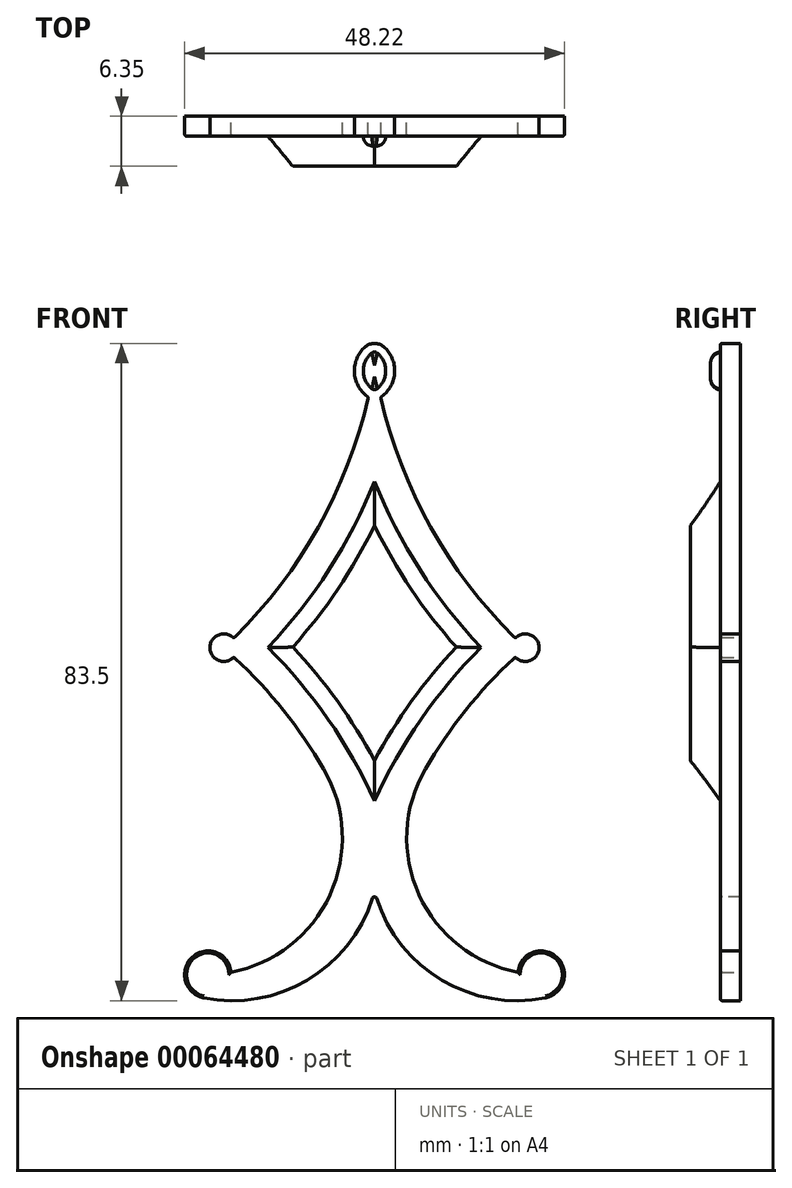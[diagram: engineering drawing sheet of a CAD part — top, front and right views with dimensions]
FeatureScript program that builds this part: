
annotation { "Feature Type Name" : "Feature", "Feature Type Description" : "" }
export const myFeature = defineFeature(function(context is Context, id is Id, definition is map)
    precondition{}
    {
        {
            var Q0;
            Q0=qCreatedBy(makeId("Front.planeOp"),FACE);
            var sketch = newSketch(context, id + "F0", { "sketchPlane" : qUnion([Q0])});
            skArc(sketch, "E0", {"start": v(-17.9, 1.2) * mm, "mid": v(-7.14, 15.28) * mm, "end": v(-0.78, 31.81) * mm});
            skArc(sketch, "E1", {"start": v(-6.45, -15.43) * mm, "mid": v(-11.63, -7.88) * mm, "end": v(-17.87, -1.17) * mm});
            skArc(sketch, "E2", {"start": v(-18.24, -41.23) * mm, "mid": v(-5.65, -31.39) * mm, "end": v(-6.45, -15.43) * mm});
            skArc(sketch, "E3", {"start": v(-17.9, 1.2) * mm, "mid": v(-20.9, -0.02) * mm, "end": v(-17.87, -1.17) * mm});
            skArc(sketch, "E4", {"start": v(-21.74, -44.48) * mm, "mid": v(-8.2, -42.03) * mm, "end": v(0, -30.98) * mm});
            skEllipticalArc(sketch, "E5", {});
            skLineSegment(sketch, "E6", {"start": v(0, 77.82) * mm, "end": v(0, -71.34) * mm, "construction": true});
            skArc(sketch, "E7.MirrorCS", {"start": v(17.9, 1.2) * mm, "mid": v(7.14, 15.28) * mm, "end": v(0.78, 31.81) * mm});
            skArc(sketch, "E8.MirrorCS", {"start": v(6.45, -15.43) * mm, "mid": v(11.63, -7.88) * mm, "end": v(17.87, -1.17) * mm});
            skArc(sketch, "E9.MirrorCS", {"start": v(18.24, -41.23) * mm, "mid": v(5.65, -31.39) * mm, "end": v(6.45, -15.43) * mm});
            skArc(sketch, "E10.MirrorCS", {"start": v(21.74, -44.48) * mm, "mid": v(8.2, -42.03) * mm, "end": v(0, -30.98) * mm});
            skEllipticalArc(sketch, "E11.MirrorC", {});
            skArc(sketch, "E12", {"start": v(0, 38.93) * mm, "mid": v(-2.54, 35.6) * mm, "end": v(-0.78, 31.81) * mm});
            skArc(sketch, "E13.MirrorCS", {"start": v(0, 38.93) * mm, "mid": v(2.54, 35.6) * mm, "end": v(0.78, 31.81) * mm});
            skPoint(sketch, "E14.orphan", {"position": v(0, -30.98) * mm});
            skPoint(sketch, "E15.orphan", {"position": v(0, 35.8) * mm});
            skArc(sketch, "E16.MirrorCS", {"start": v(17.9, 1.2) * mm, "mid": v(20.9, -0.02) * mm, "end": v(17.87, -1.17) * mm});
            const initialGuessF0  = {"E5": [-0.02116856537759304, -0.04152892157435417, 1, 0, 0.002945323460980625, 0.0030059937877719195, 0.09832466558772346, 4.51858815046972], "E11.MirrorC": [0.02116856537759304, -0.04152892157435417, -1, 0, 0.002945323460980625, 0.0030059937877719195, 1.764597156709867, 6.184860641591863], "E11.MirrorC": [0.02116856537759304, -0.04152892157435417, -1, 0, 0.002945323460980625, 0.0030059937877719195, 1.764597156709867, 6.1848606415918645]};
            skSetInitialGuess(sketch, initialGuessF0);
            skSolve(sketch);
        }
        {
            var Q0;
            Q0 = qSketchRegion(id + "F0", true);
            extrude(context, id + "F1", {"entities" : qUnion([Q0]), "depth" : 2.54 * mm});
        }
        {
            var Q0;
            Q0=makeQuery(id+"F1.opExtrude","CAP_FACE",FACE,{"disambiguationData":[OSD([sQuery(id+"F0.wireOp",EDGE,"E0"),sQuery(id+"F0.wireOp",EDGE,"E1"),sQuery(id+"F0.wireOp",EDGE,"E2"),sQuery(id+"F0.wireOp",EDGE,"E3"),sQuery(id+"F0.wireOp",EDGE,"E4"),sQuery(id+"F0.wireOp",EDGE,"E5"),sQuery(id+"F0.wireOp",EDGE,"E7.MirrorCS"),sQuery(id+"F0.wireOp",EDGE,"E8.MirrorCS"),sQuery(id+"F0.wireOp",EDGE,"E12"),sQuery(id+"F0.wireOp",EDGE,"E13.MirrorCS"),sQuery(id+"F0.wireOp",EDGE,"E16.MirrorCS"),sQuery(id+"F0.wireOp",EDGE,"E10.MirrorCS"),sQuery(id+"F0.wireOp",EDGE,"E11.MirrorC"),sQuery(id+"F0.wireOp",EDGE,"E9.MirrorCS")])],"isStart":false});
            var sketch = newSketch(context, id + "F2", { "sketchPlane" : qUnion([Q0])});
            skArc(sketch, "E17", {"start": v(-15.68, 0) * mm, "mid": v(-6.34, 11.87) * mm, "end": v(0, 25.58) * mm});
            skArc(sketch, "E18", {"start": v(0, -23.4) * mm, "mid": v(-6.55, -10.83) * mm, "end": v(-15.68, 0) * mm});
            skArc(sketch, "E19.MirrorCS", {"start": v(15.68, 0) * mm, "mid": v(6.34, 11.87) * mm, "end": v(0, 25.58) * mm});
            skArc(sketch, "E20.MirrorCS", {"start": v(0, -23.4) * mm, "mid": v(6.55, -10.83) * mm, "end": v(15.68, 0) * mm});
            skSolve(sketch);
        }
        {
            var Q0;
            Q0 = qSketchRegion(id + "F2", true);
            extrude(context, id + "F3", {"entities" : qUnion([Q0]), "operationType" : NewBodyOperationType.ADD, "depth" : 3.8 * mm});
        }
        {
            var Q0;
            Q0=makeQuery(id+"F3.opExtrude","CAP_EDGE",EDGE,{"disambiguationData":[OSD([sQuery(id+"F2.wireOp",EDGE,"E19.MirrorCS")])],"isStart":false});
            var Q1;
            Q1=makeQuery(id+"F3.opExtrude","CAP_EDGE",EDGE,{"disambiguationData":[OSD([sQuery(id+"F2.wireOp",EDGE,"E20.MirrorCS")])],"isStart":false});
            var Q2;
            Q2=makeQuery(id+"F3.opExtrude","CAP_EDGE",EDGE,{"disambiguationData":[OSD([sQuery(id+"F2.wireOp",EDGE,"E17")])],"isStart":false});
            var Q3;
            Q3=makeQuery(id+"F3.opExtrude","CAP_EDGE",EDGE,{"disambiguationData":[OSD([sQuery(id+"F2.wireOp",EDGE,"E18")])],"isStart":false});
            chamfer(context, id + "F4", {"entities" : qUnion([Q0, Q1, Q2, Q3]), "chamferType" : ChamferType.TWO_OFFSETS, "width1" : 6.35 * mm, "oppositeDirection" : false, "width2" : 3.8 * mm, "tangentPropagation" : true});
        }
        {
            var Q0;
            Q0=makeQuery(id+"F1.opExtrude","CAP_EDGE",EDGE,{"disambiguationData":[OSD([sQuery(id+"F0.wireOp",EDGE,"E2")])],"isStart":false});
            var Q1;
            Q1=makeQuery(id+"F1.opExtrude","CAP_EDGE",EDGE,{"disambiguationData":[OSD([sQuery(id+"F0.wireOp",EDGE,"E1")])],"isStart":false});
            var Q2;
            Q2=makeQuery(id+"F1.opExtrude","CAP_EDGE",EDGE,{"disambiguationData":[OSD([sQuery(id+"F0.wireOp",EDGE,"E3")])],"isStart":false});
            var Q3;
            Q3=makeQuery(id+"F1.opExtrude","CAP_EDGE",EDGE,{"disambiguationData":[OSD([sQuery(id+"F0.wireOp",EDGE,"E9.MirrorCS")])],"isStart":false});
            var Q4;
            Q4=makeQuery(id+"F1.opExtrude","CAP_EDGE",EDGE,{"disambiguationData":[OSD([sQuery(id+"F0.wireOp",EDGE,"E5")])],"isStart":false});
            var Q5;
            Q5=makeQuery(id+"F1.opExtrude","CAP_EDGE",EDGE,{"disambiguationData":[OSD([sQuery(id+"F0.wireOp",EDGE,"E4")])],"isStart":false});
            var Q6;
            Q6=makeQuery(id+"F1.opExtrude","CAP_EDGE",EDGE,{"disambiguationData":[OSD([sQuery(id+"F0.wireOp",EDGE,"E10.MirrorCS")])],"isStart":false});
            var Q7;
            Q7=makeQuery(id+"F1.opExtrude","CAP_EDGE",EDGE,{"disambiguationData":[OSD([sQuery(id+"F0.wireOp",EDGE,"E11.MirrorC")])],"isStart":false});
            var Q8;
            Q8=makeQuery(id+"F1.opExtrude","CAP_EDGE",EDGE,{"disambiguationData":[OSD([sQuery(id+"F0.wireOp",EDGE,"E8.MirrorCS")])],"isStart":false});
            var Q9;
            Q9=makeQuery(id+"F1.opExtrude","CAP_EDGE",EDGE,{"disambiguationData":[OSD([sQuery(id+"F0.wireOp",EDGE,"E16.MirrorCS")])],"isStart":false});
            var Q10;
            Q10=makeQuery(id+"F1.opExtrude","CAP_EDGE",EDGE,{"disambiguationData":[OSD([sQuery(id+"F0.wireOp",EDGE,"E7.MirrorCS")])],"isStart":false});
            var Q11;
            Q11=makeQuery(id+"F1.opExtrude","CAP_EDGE",EDGE,{"disambiguationData":[OSD([sQuery(id+"F0.wireOp",EDGE,"E12")])],"isStart":false});
            var Q12;
            Q12=makeQuery(id+"F1.opExtrude","CAP_EDGE",EDGE,{"disambiguationData":[OSD([sQuery(id+"F0.wireOp",EDGE,"E13.MirrorCS")])],"isStart":false});
            var Q13;
            Q13=makeQuery(id+"F1.opExtrude","CAP_EDGE",EDGE,{"disambiguationData":[OSD([sQuery(id+"F0.wireOp",EDGE,"E0")])],"isStart":false});
            var Q14;
            Q14=makeQuery(id+"F1.opExtrude","SWEPT_EDGE",EDGE,{"disambiguationData":[OSD([sQuery(id+"F0.wireOp",EDGE,"E0"),sQuery(id+"F0.wireOp",EDGE,"E12")])]});
            var Q15;
            Q15=makeQuery(id+"F1.opExtrude","SWEPT_EDGE",EDGE,{"disambiguationData":[OSD([sQuery(id+"F0.wireOp",EDGE,"E7.MirrorCS"),sQuery(id+"F0.wireOp",EDGE,"E13.MirrorCS")])]});
            var Q16;
            Q16=makeQuery(id+"F1.opExtrude","SWEPT_EDGE",EDGE,{"disambiguationData":[OSD([sQuery(id+"F0.wireOp",EDGE,"E7.MirrorCS"),sQuery(id+"F0.wireOp",EDGE,"E16.MirrorCS")])]});
            var Q17;
            Q17=makeQuery(id+"F1.opExtrude","SWEPT_EDGE",EDGE,{"disambiguationData":[OSD([sQuery(id+"F0.wireOp",EDGE,"E8.MirrorCS"),sQuery(id+"F0.wireOp",EDGE,"E16.MirrorCS")])]});
            var Q18;
            Q18=makeQuery(id+"F1.opExtrude","SWEPT_EDGE",EDGE,{"disambiguationData":[OSD([sQuery(id+"F0.wireOp",EDGE,"E4"),sQuery(id+"F0.wireOp",EDGE,"E10.MirrorCS")])]});
            var Q19;
            Q19=makeQuery(id+"F1.opExtrude","SWEPT_EDGE",EDGE,{"disambiguationData":[OSD([sQuery(id+"F0.wireOp",EDGE,"E0"),sQuery(id+"F0.wireOp",EDGE,"E3")])]});
            var Q20;
            Q20=makeQuery(id+"F1.opExtrude","SWEPT_EDGE",EDGE,{"disambiguationData":[OSD([sQuery(id+"F0.wireOp",EDGE,"E1"),sQuery(id+"F0.wireOp",EDGE,"E3")])]});
            fillet(context, id + "F5", {"entities" : qUnion([Q0, Q1, Q2, Q3, Q4, Q5, Q6, Q7, Q8, Q9, Q10, Q11, Q12, Q13, Q14, Q15, Q16, Q17, Q18, Q19, Q20]), "radius" : 0.25 * mm, "tangentPropagation" : true, "allowEdgeOverflow" : false});
        }
        {
            var Q0;
            Q0=makeQuery(id+"F1.opExtrude","SWEPT_EDGE",EDGE,{"disambiguationData":[OSD([sQuery(id+"F0.wireOp",EDGE,"E12"),sQuery(id+"F0.wireOp",EDGE,"E13.MirrorCS")])]});
            fillet(context, id + "F6", {"entities" : qUnion([Q0]), "radius" : 1.78 * mm, "tangentPropagation" : true, "allowEdgeOverflow" : false});
        }
        {
            var Q0;
            Q0=makeQuery(id+"F1.opExtrude","CAP_FACE",FACE,{"disambiguationData":[OSD([sQuery(id+"F0.wireOp",EDGE,"E0"),sQuery(id+"F0.wireOp",EDGE,"E1"),sQuery(id+"F0.wireOp",EDGE,"E2"),sQuery(id+"F0.wireOp",EDGE,"E3"),sQuery(id+"F0.wireOp",EDGE,"E4"),sQuery(id+"F0.wireOp",EDGE,"E5"),sQuery(id+"F0.wireOp",EDGE,"E7.MirrorCS"),sQuery(id+"F0.wireOp",EDGE,"E8.MirrorCS"),sQuery(id+"F0.wireOp",EDGE,"E12"),sQuery(id+"F0.wireOp",EDGE,"E13.MirrorCS"),sQuery(id+"F0.wireOp",EDGE,"E16.MirrorCS"),sQuery(id+"F0.wireOp",EDGE,"E10.MirrorCS"),sQuery(id+"F0.wireOp",EDGE,"E11.MirrorC"),sQuery(id+"F0.wireOp",EDGE,"E9.MirrorCS")])],"isStart":false});
            var sketch = newSketch(context, id + "F7", { "sketchPlane" : qUnion([Q0])});
            skArc(sketch, "E21", {"start": v(0, 32.67) * mm, "mid": v(1.42, 35.17) * mm, "end": v(0, 37.67) * mm});
            skArc(sketch, "E22", {"start": v(0, 37.67) * mm, "mid": v(-1.42, 35.17) * mm, "end": v(0, 32.67) * mm});
            skSolve(sketch);
        }
        {
            var Q0;
            Q0 = qSketchRegion(id + "F7", true);
            extrude(context, id + "F8", {"entities" : qUnion([Q0]), "operationType" : NewBodyOperationType.ADD, "depth" : 1.27 * mm});
        }
        {
            var Q0;
            Q0=makeQuery(id+"F8.opExtrude","CAP_EDGE",EDGE,{"disambiguationData":[OSD([sQuery(id+"F7.wireOp",EDGE,"E22")])],"isStart":false});
            var Q1;
            Q1=makeQuery(id+"F8.opExtrude","CAP_EDGE",EDGE,{"disambiguationData":[OSD([sQuery(id+"F7.wireOp",EDGE,"E21")])],"isStart":false});
            fillet(context, id + "F9", {"entities" : qUnion([Q0, Q1]), "radius" : 1.27 * mm, "tangentPropagation" : true, "allowEdgeOverflow" : false});
        }
        {
            var Q0;
            Q0=makeQuery(id+"F9.opFillet","BLEND_EDGE",EDGE,{"disambiguationData":[OD(1.0)],"blendedFrom":[makeQuery(id+"F8.opExtrude","CAP_EDGE",EDGE,{"disambiguationData":[OSD([sQuery(id+"F7.wireOp",EDGE,"E21")])],"isStart":false}),makeQuery(id+"F8.opExtrude","CAP_EDGE",EDGE,{"disambiguationData":[OSD([sQuery(id+"F7.wireOp",EDGE,"E22")])],"isStart":false})],"blendedInto":[]});
            var Q1;
            Q1=makeQuery(id+"F9.opFillet","BLEND_EDGE",EDGE,{"disambiguationData":[OD(0.0)],"blendedFrom":[makeQuery(id+"F8.opExtrude","CAP_EDGE",EDGE,{"disambiguationData":[OSD([sQuery(id+"F7.wireOp",EDGE,"E21")])],"isStart":false}),makeQuery(id+"F8.opExtrude","CAP_EDGE",EDGE,{"disambiguationData":[OSD([sQuery(id+"F7.wireOp",EDGE,"E22")])],"isStart":false})],"blendedInto":[]});
            fillet(context, id + "F10", {"entities" : qUnion([Q0, Q1]), "radius" : 0.5 * mm, "tangentPropagation" : true, "allowEdgeOverflow" : false});
        }
    });
